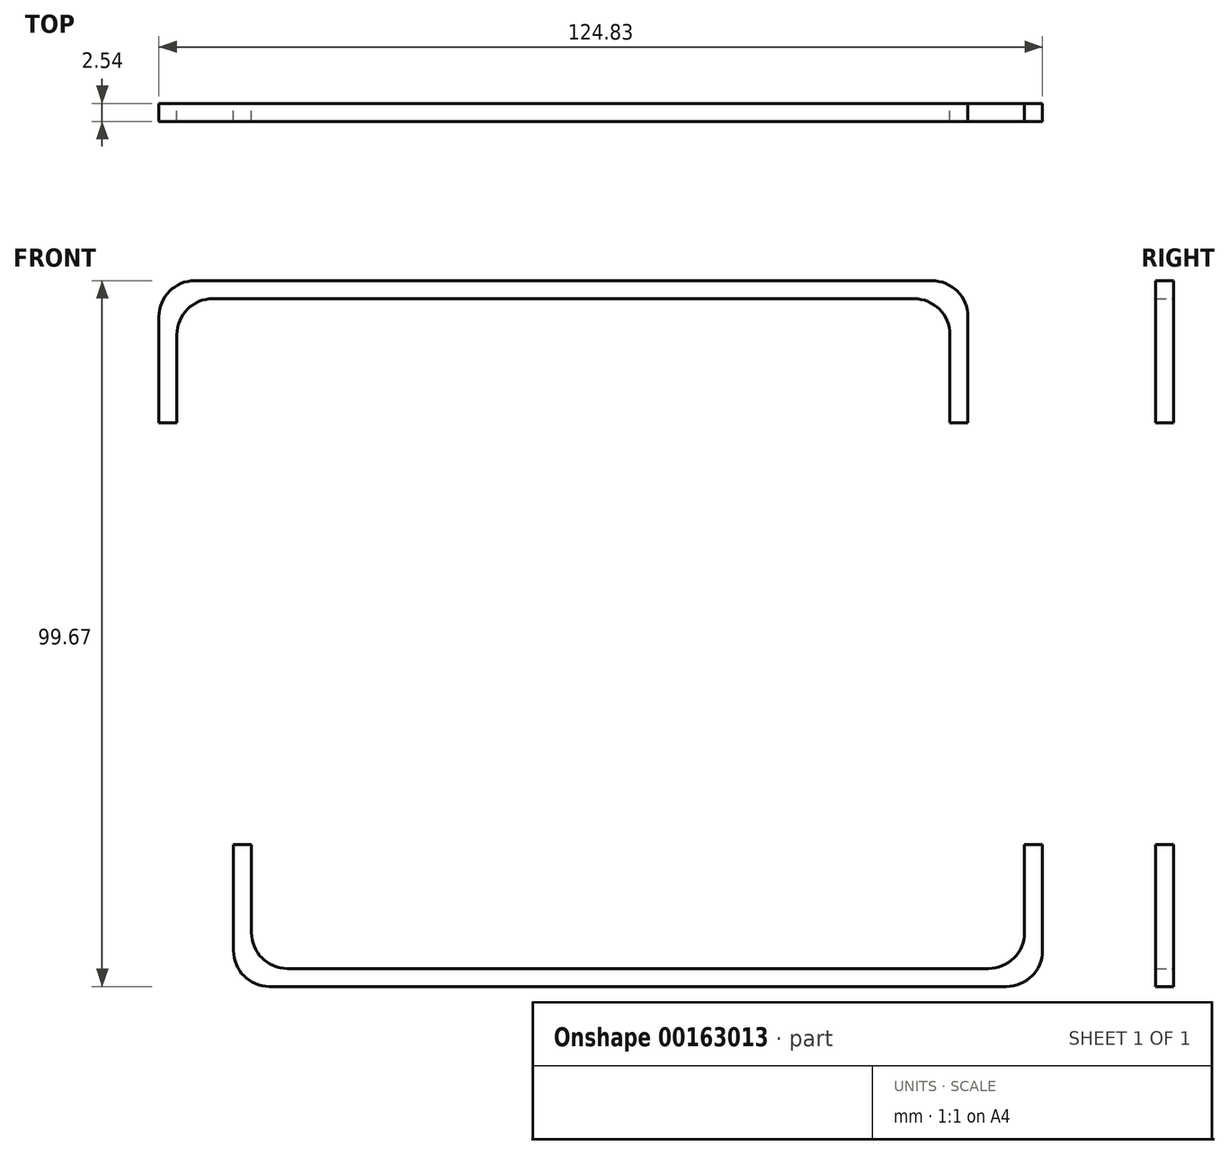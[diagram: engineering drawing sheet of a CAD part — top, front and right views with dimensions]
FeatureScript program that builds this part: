
annotation { "Feature Type Name" : "Feature", "Feature Type Description" : "" }
export const myFeature = defineFeature(function(context is Context, id is Id, definition is map)
    precondition{}
    {
        {
            var Q0;
            Q0=qCreatedBy(makeId("Front.planeOp"),FACE);
            var sketch = newSketch(context, id + "F0", { "sketchPlane" : qUnion([Q0])});
            skLineSegment(sketch, "E0.bottom", {"start": v(-59.36, 57.6) * mm, "end": v(-56.82, 57.6) * mm});
            skLineSegment(sketch, "E0.top", {"start": v(-59.36, 40.08) * mm, "end": v(-56.82, 40.08) * mm});
            skLineSegment(sketch, "E0.left", {"start": v(-59.36, 57.6) * mm, "end": v(-59.36, 40.08) * mm});
            skLineSegment(sketch, "E0.right", {"start": v(-56.82, 57.6) * mm, "end": v(-56.82, 40.08) * mm});
            skLineSegment(sketch, "E1.bottom", {"start": v(-59.36, 57.6) * mm, "end": v(54.94, 57.6) * mm});
            skLineSegment(sketch, "E1.top", {"start": v(-59.36, 60.14) * mm, "end": v(54.94, 60.14) * mm});
            skLineSegment(sketch, "E1.left", {"start": v(-59.36, 57.6) * mm, "end": v(-59.36, 60.14) * mm});
            skLineSegment(sketch, "E1.right", {"start": v(54.94, 57.6) * mm, "end": v(54.94, 60.14) * mm});
            skLineSegment(sketch, "E2.bottom", {"start": v(54.94, 57.6) * mm, "end": v(52.4, 57.6) * mm});
            skLineSegment(sketch, "E2.top", {"start": v(54.94, 40.08) * mm, "end": v(52.4, 40.08) * mm});
            skLineSegment(sketch, "E2.left", {"start": v(54.94, 57.6) * mm, "end": v(54.94, 40.08) * mm});
            skLineSegment(sketch, "E2.right", {"start": v(52.4, 57.6) * mm, "end": v(52.4, 40.08) * mm});
            skLineSegment(sketch, "E3.bottom", {"start": v(-48.83, -37) * mm, "end": v(65.47, -37) * mm});
            skLineSegment(sketch, "E3.top", {"start": v(-48.83, -39.53) * mm, "end": v(65.47, -39.53) * mm});
            skLineSegment(sketch, "E3.left", {"start": v(-48.83, -37) * mm, "end": v(-48.83, -39.53) * mm});
            skLineSegment(sketch, "E3.right", {"start": v(65.47, -37) * mm, "end": v(65.47, -39.53) * mm});
            skLineSegment(sketch, "E4.bottom", {"start": v(-48.83, -37) * mm, "end": v(-46.29, -37) * mm});
            skLineSegment(sketch, "E4.top", {"start": v(-48.83, -19.47) * mm, "end": v(-46.29, -19.47) * mm});
            skLineSegment(sketch, "E4.left", {"start": v(-48.83, -37) * mm, "end": v(-48.83, -19.47) * mm});
            skLineSegment(sketch, "E4.right", {"start": v(-46.29, -37) * mm, "end": v(-46.29, -19.47) * mm});
            skLineSegment(sketch, "E5.bottom", {"start": v(65.47, -37) * mm, "end": v(62.93, -37) * mm});
            skLineSegment(sketch, "E5.top", {"start": v(65.47, -19.47) * mm, "end": v(62.93, -19.47) * mm});
            skLineSegment(sketch, "E5.left", {"start": v(65.47, -37) * mm, "end": v(65.47, -19.47) * mm});
            skLineSegment(sketch, "E5.right", {"start": v(62.93, -37) * mm, "end": v(62.93, -19.47) * mm});
            skSolve(sketch);
        }
        {
            var Q0;
            Q0 = qSketchRegion(id + "F0", true);
            extrude(context, id + "F1", {"entities" : qUnion([Q0]), "depth" : 2.54 * mm});
        }
        {
            var Q0;
            Q0=makeQuery(id+"F1.opExtrude","SWEPT_EDGE",EDGE,{"disambiguationData":[OSD([sQuery(id+"F0.wireOp",EDGE,"E3.bottom"),sQuery(id+"F0.wireOp",EDGE,"E4.bottom"),sQuery(id+"F0.wireOp",EDGE,"E4.right")])]});
            var Q1;
            Q1=makeQuery(id+"F1.opExtrude","SWEPT_EDGE",EDGE,{"disambiguationData":[OSD([sQuery(id+"F0.wireOp",EDGE,"E3.top"),sQuery(id+"F0.wireOp",EDGE,"E3.left")])]});
            var Q2;
            Q2=makeQuery(id+"F1.opExtrude","SWEPT_EDGE",EDGE,{"disambiguationData":[OSD([sQuery(id+"F0.wireOp",EDGE,"E3.bottom"),sQuery(id+"F0.wireOp",EDGE,"E5.bottom"),sQuery(id+"F0.wireOp",EDGE,"E5.right")])]});
            var Q3;
            Q3=makeQuery(id+"F1.opExtrude","SWEPT_EDGE",EDGE,{"disambiguationData":[OSD([sQuery(id+"F0.wireOp",EDGE,"E3.top"),sQuery(id+"F0.wireOp",EDGE,"E3.right")])]});
            var Q4;
            Q4=makeQuery(id+"F1.opExtrude","SWEPT_EDGE",EDGE,{"disambiguationData":[OSD([sQuery(id+"F0.wireOp",EDGE,"E1.bottom"),sQuery(id+"F0.wireOp",EDGE,"E2.bottom"),sQuery(id+"F0.wireOp",EDGE,"E2.right")])]});
            var Q5;
            Q5=makeQuery(id+"F1.opExtrude","SWEPT_EDGE",EDGE,{"disambiguationData":[OSD([sQuery(id+"F0.wireOp",EDGE,"E1.top"),sQuery(id+"F0.wireOp",EDGE,"E1.right")])]});
            var Q6;
            Q6=makeQuery(id+"F1.opExtrude","SWEPT_EDGE",EDGE,{"disambiguationData":[OSD([sQuery(id+"F0.wireOp",EDGE,"E0.right"),sQuery(id+"F0.wireOp",EDGE,"E1.bottom")])]});
            var Q7;
            Q7=makeQuery(id+"F1.opExtrude","SWEPT_EDGE",EDGE,{"disambiguationData":[OSD([sQuery(id+"F0.wireOp",EDGE,"E1.top"),sQuery(id+"F0.wireOp",EDGE,"E1.left")])]});
            fillet(context, id + "F2", {"entities" : qUnion([Q0, Q1, Q2, Q3, Q4, Q5, Q6, Q7]), "radius" : 5.08 * mm, "tangentPropagation" : true, "allowEdgeOverflow" : false});
        }
    });
